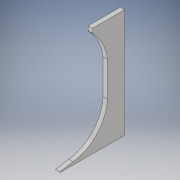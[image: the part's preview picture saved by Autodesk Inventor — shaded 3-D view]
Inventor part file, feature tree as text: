
AUTODESK INVENTOR PART (.ipt)
format: ipt  version: 2018 (Build 220112000, 112)  size: 133,120 bytes
history: native  units: in
note: dims shown in document units (in); Inventor stores cm internally (conversion verified against a paired STEP export)
features: fillet x2, extrude x1, sketch x1
ambient origin geometry x8: Origin, YZ Plane, XZ Plane, XY Plane, X Axis, Y Axis, Z Axis, Center Point
bodies: Solid1 (feature_tree)
feature tree (4):
  extrude  "Extrusion1"  Depth=12.0in
  fillet  "Fillet1"  Radius=19.0in
  fillet  "Fillet2"  Radius=3.0in
  sketch  "Sketch1"  dims[d0=13.0in d1=12.0in d2=19.0in d3=3.0in d4=6.0in d5=8.25in d9=9.0in d13=8.625in d16=0.268in d17=0.134in d19=3.0in d20=3.0in d25=0.5in d39=7.5in d40=6.0in d41=0.5in d42=6.375in d43=135.0deg d44=7.0in d45=0.75in d46=0.0in d47=0.0625in d48=0.125in]
